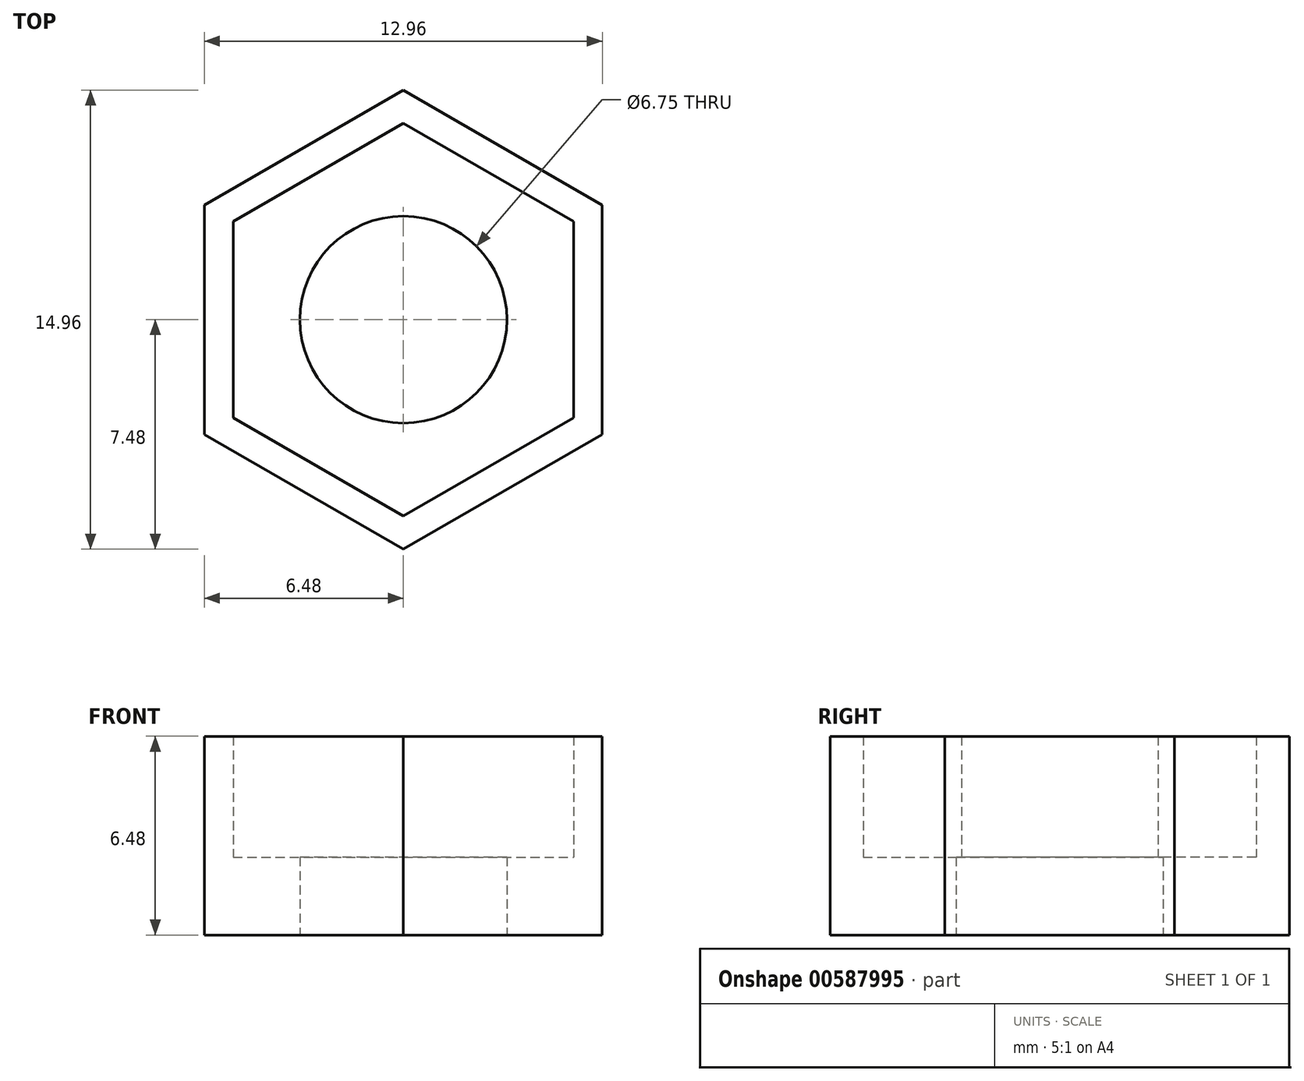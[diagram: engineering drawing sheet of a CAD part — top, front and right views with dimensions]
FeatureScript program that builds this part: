
annotation { "Feature Type Name" : "Feature", "Feature Type Description" : "" }
export const myFeature = defineFeature(function(context is Context, id is Id, definition is map)
    precondition{}
    {
        {
            var Q0;
            Q0=qCreatedBy(makeId("Top.planeOp"),FACE);
            var sketch = newSketch(context, id + "F0", { "sketchPlane" : qUnion([Q0])});
            skCircle(sketch, "E0.cCircle", {"center": v(0, 0) * mm, "radius": 5.54 * mm, "construction": true});
            skLineSegment(sketch, "E0.0", {"start": v(5.54, 3.2) * mm, "end": v(5.54, -3.2) * mm});
            skLineSegment(sketch, "E0.1", {"start": v(5.54, -3.2) * mm, "end": v(0, -6.4) * mm});
            skLineSegment(sketch, "E0.2", {"start": v(0, -6.4) * mm, "end": v(-5.54, -3.2) * mm});
            skLineSegment(sketch, "E0.3", {"start": v(-5.54, -3.2) * mm, "end": v(-5.54, 3.2) * mm});
            skLineSegment(sketch, "E0.4", {"start": v(-5.54, 3.2) * mm, "end": v(0, 6.4) * mm});
            skLineSegment(sketch, "E0.5", {"start": v(0, 6.4) * mm, "end": v(5.54, 3.2) * mm});
            skPoint(sketch, "E0.0.midPoint", {"position": v(5.54, 0) * mm});
            skCircle(sketch, "E1.cCircle", {"center": v(0, 0) * mm, "radius": 6.48 * mm, "construction": true});
            skLineSegment(sketch, "E1.0", {"start": v(6.48, 3.74) * mm, "end": v(6.48, -3.74) * mm});
            skLineSegment(sketch, "E1.1", {"start": v(6.48, -3.74) * mm, "end": v(0, -7.48) * mm});
            skLineSegment(sketch, "E1.2", {"start": v(0, -7.48) * mm, "end": v(-6.48, -3.74) * mm});
            skLineSegment(sketch, "E1.3", {"start": v(-6.48, -3.74) * mm, "end": v(-6.48, 3.74) * mm});
            skLineSegment(sketch, "E1.4", {"start": v(-6.48, 3.74) * mm, "end": v(0, 7.48) * mm});
            skLineSegment(sketch, "E1.5", {"start": v(0, 7.48) * mm, "end": v(6.48, 3.74) * mm});
            skPoint(sketch, "E1.0.midPoint", {"position": v(6.48, 0) * mm});
            skCircle(sketch, "E2", {"center": v(0, 0) * mm, "radius": 3.37 * mm});
            skSolve(sketch);
        }
        {
            var Q0;
            Q0=makeQuery(id+"F0.imprint","IMPRINT",FACE,{"disambiguationData":[TD([[makeQuery(id+"F0.imprint","IMPRINT",EDGE,{"derivedFrom":sQuery(id+"F0.wireOp",EDGE,"E0.0")}),-1.0]])]});
            extrude(context, id + "F1", {"entities" : qUnion([Q0]), "depth" : 2.54 * mm, "offsetDistance" : 25.4 * mm});
        }
        {
            var Q0;
            Q0=makeQuery(id+"F0.imprint","IMPRINT",FACE,{"disambiguationData":[TD([[makeQuery(id+"F0.imprint","IMPRINT",EDGE,{"derivedFrom":sQuery(id+"F0.wireOp",EDGE,"E0.0")}),1.0]])]});
            extrude(context, id + "F2", {"entities" : qUnion([Q0]), "operationType" : NewBodyOperationType.ADD, "depth" : 6.48 * mm, "offsetDistance" : 25.4 * mm});
        }
    });
